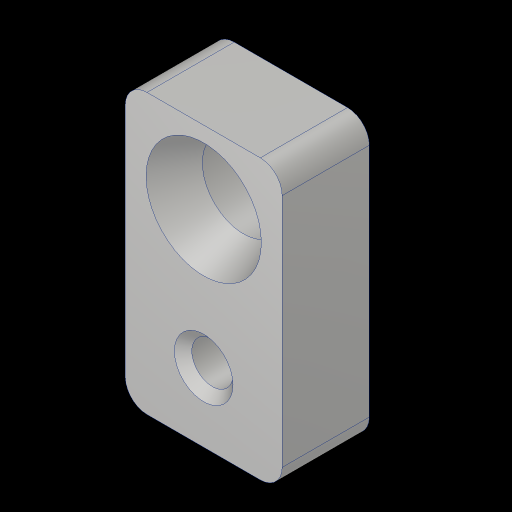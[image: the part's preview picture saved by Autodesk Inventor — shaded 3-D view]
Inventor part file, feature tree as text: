
AUTODESK INVENTOR PART (.ipt)
format: ipt  version: 2023.3 (Build 273359000, 359)  size: 278,016 bytes
history: native  units: in
note: dims shown in document units (in); Inventor stores cm internally (conversion verified against a paired STEP export)
features: sketch x4, extrude x2, hole x2, fillet x1, chamfer x1
ambient origin geometry x8: Origin, YZ Plane, XZ Plane, XY Plane, X Axis, Y Axis, Z Axis, Center Point
bodies: Solid1 (feature_tree)
feature tree (10):
  extrude  "Extrusion1"  Depth=0.45in
  hole  "Hole1"  [1 undecoded]
  hole  "Hole2"  [1 undecoded]
  fillet  "Fillet1"  Radius=0.225in
  extrude  "Extrusion2"  Depth=0.05in
  chamfer  "Chamfer2"  Distance=0.0625in
  sketch  "Sketch1"  dims[d0=0.8in d1=0.45in]
  sketch  "Sketch2"  dims[d2=0.25in d3=0.0in d5=0.197in]
  sketch  "Sketch3"  dims[d6=0.1181in d7=0.75in d8=0.332in d9=0.25in d10=0.5635in d11=1.0in d12=0.8108in d13=0.5909in d14=0.225in]
  sketch  "Sketch4"  dims[d15=0.2362in d16=0.75in d17=0.3307in d18=0.25in d19=45.0deg d20=1.0in d21=0.8108in d22=0.225in d23=0.0625in d27=0.3071in d28=0.05in d29=0.0in d30=0.025in d31=0.125in d32=45.0deg]
note: 2 required parameter values undecoded (feature->parameter linkage not recoverable at this tier; creation-order binding heuristic only, values carry confidence <= 0.55)
